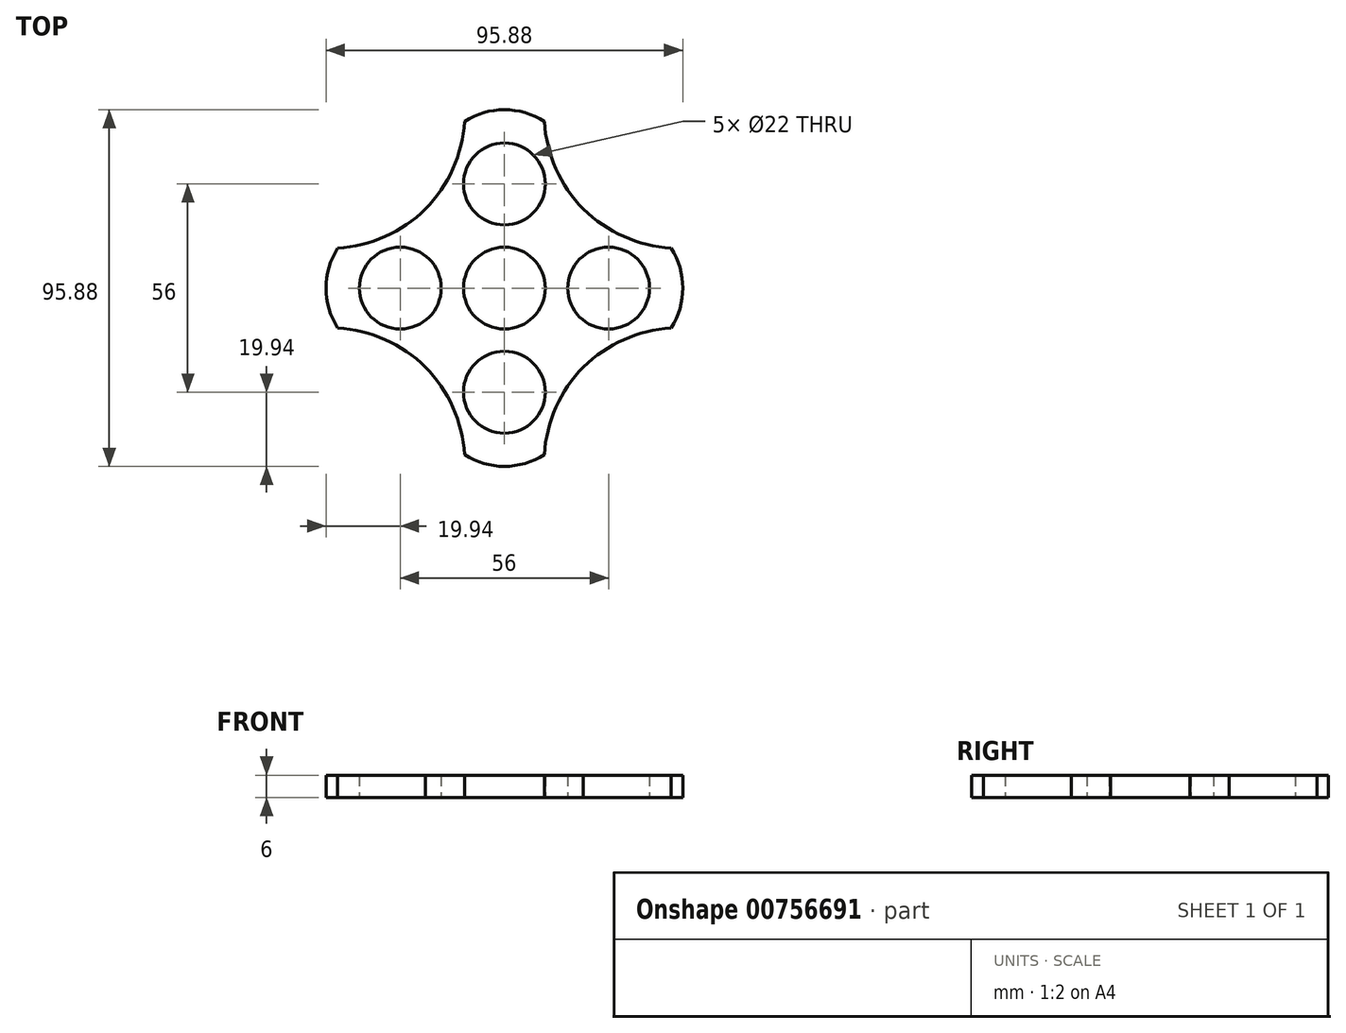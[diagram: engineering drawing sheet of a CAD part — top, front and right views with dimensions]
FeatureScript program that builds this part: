
annotation { "Feature Type Name" : "Feature", "Feature Type Description" : "" }
export const myFeature = defineFeature(function(context is Context, id is Id, definition is map)
    precondition{}
    {
        {
            var Q0;
            Q0=qCreatedBy(makeId("Top.planeOp"),FACE);
            var sketch = newSketch(context, id + "F0", { "sketchPlane" : qUnion([Q0])});
            skCircle(sketch, "E0", {"center": v(0, 0) * mm, "radius": 11 * mm});
            skArc(sketch, "E1", {"start": v(4.77, 18.09) * mm, "mid": v(0, 39) * mm, "end": v(-4.77, 18.09) * mm});
            skArc(sketch, "E2", {"start": v(-22.32, 20.14) * mm, "mid": v(-14.18, 31.38) * mm, "end": v(-10.7, 44.82) * mm});
            skArc(sketch, "E3.MirrorCS", {"start": v(22.32, 20.14) * mm, "mid": v(14.18, 31.38) * mm, "end": v(10.7, 44.82) * mm});
            skArc(sketch, "E4", {"start": v(-10.7, 44.82) * mm, "mid": v(0, 47.94) * mm, "end": v(10.7, 44.82) * mm});
            skArc(sketch, "E5.1.0", {"start": v(-18.09, 4.77) * mm, "mid": v(-39, 0) * mm, "end": v(-18.09, -4.77) * mm});
            skArc(sketch, "E5.1.1", {"start": v(-20.14, 22.32) * mm, "mid": v(-31.38, 14.18) * mm, "end": v(-44.82, 10.7) * mm});
            skArc(sketch, "E5.1.2", {"start": v(-44.82, -10.7) * mm, "mid": v(-47.94, 0) * mm, "end": v(-44.82, 10.7) * mm});
            skArc(sketch, "E5.1.3", {"start": v(-20.14, -22.32) * mm, "mid": v(-31.38, -14.18) * mm, "end": v(-44.82, -10.7) * mm});
            skArc(sketch, "E5.2.0", {"start": v(-4.77, -18.09) * mm, "mid": v(0, -39) * mm, "end": v(4.77, -18.09) * mm});
            skArc(sketch, "E5.2.1", {"start": v(-22.32, -20.14) * mm, "mid": v(-14.18, -31.38) * mm, "end": v(-10.7, -44.82) * mm});
            skArc(sketch, "E5.2.2", {"start": v(10.7, -44.82) * mm, "mid": v(0, -47.94) * mm, "end": v(-10.7, -44.82) * mm});
            skArc(sketch, "E5.2.3", {"start": v(22.32, -20.14) * mm, "mid": v(14.18, -31.38) * mm, "end": v(10.7, -44.82) * mm});
            skArc(sketch, "E5.3.0", {"start": v(18.09, -4.77) * mm, "mid": v(39, 0) * mm, "end": v(18.09, 4.77) * mm});
            skArc(sketch, "E5.3.1", {"start": v(20.14, -22.32) * mm, "mid": v(31.38, -14.18) * mm, "end": v(44.82, -10.7) * mm});
            skArc(sketch, "E5.3.2", {"start": v(44.82, 10.7) * mm, "mid": v(47.94, 0) * mm, "end": v(44.82, -10.7) * mm});
            skArc(sketch, "E5.3.3", {"start": v(20.14, 22.32) * mm, "mid": v(31.38, 14.18) * mm, "end": v(44.82, 10.7) * mm});
            skArc(sketch, "E6", {"start": v(-18.09, 4.77) * mm, "mid": v(-17, 0) * mm, "end": v(-18.09, -4.77) * mm});
            skArc(sketch, "E7", {"start": v(4.77, 18.09) * mm, "mid": v(0, 17) * mm, "end": v(-4.77, 18.09) * mm});
            skArc(sketch, "E8", {"start": v(18.09, 4.77) * mm, "mid": v(17, 0) * mm, "end": v(18.09, -4.77) * mm});
            skArc(sketch, "E9", {"start": v(-4.77, -18.09) * mm, "mid": v(0, -17) * mm, "end": v(4.77, -18.09) * mm});
            skSolve(sketch);
        }
        {
            var Q0;
            Q0=makeQuery(id+"F0.imprint","IMPRINT",FACE,{"disambiguationData":[TD([[makeQuery(id+"F0.imprint","IMPRINT",EDGE,{"derivedFrom":sQuery(id+"F0.wireOp",EDGE,"E0")}),-1.0]])]});
            extrude(context, id + "F1", {"entities" : qUnion([Q0]), "depth" : 6 * mm, "offsetDistance" : 25 * mm});
        }
    });
